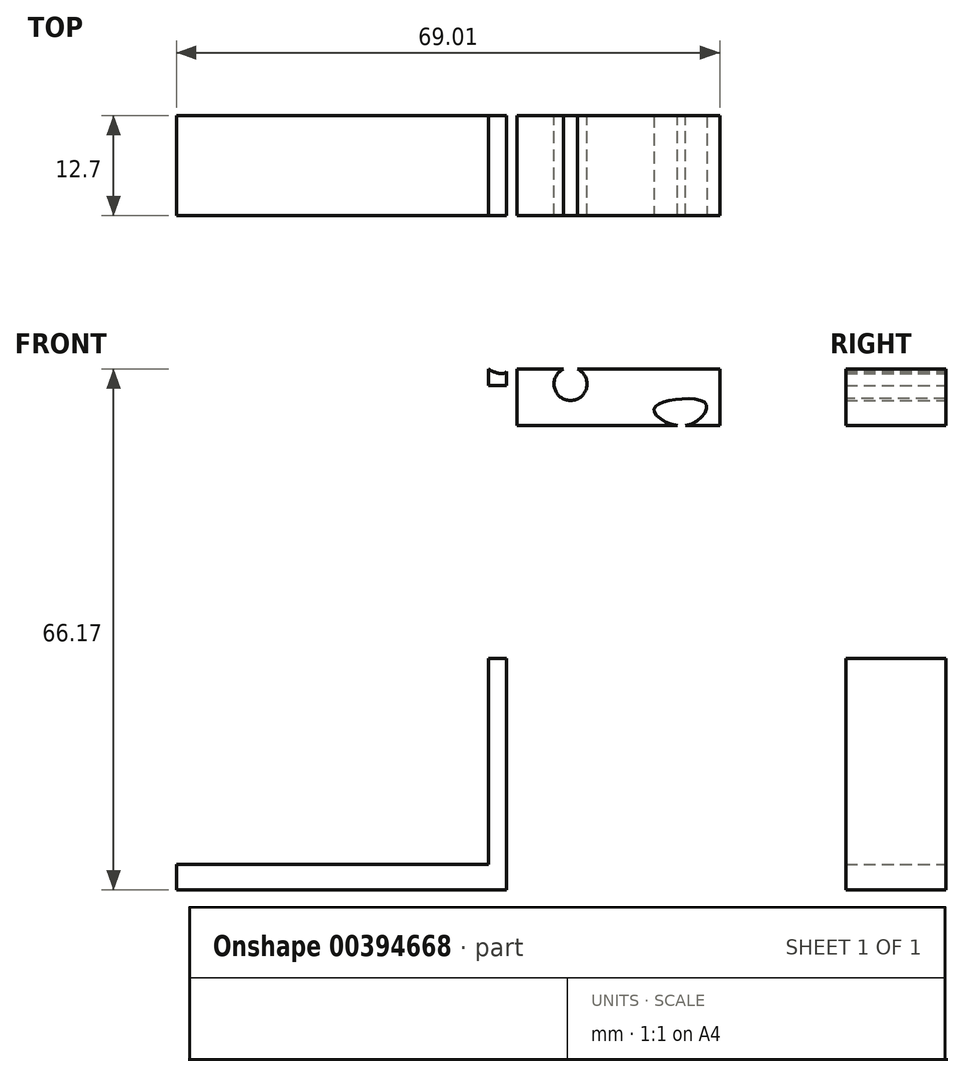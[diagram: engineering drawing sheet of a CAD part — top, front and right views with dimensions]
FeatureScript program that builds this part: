
annotation { "Feature Type Name" : "Feature", "Feature Type Description" : "" }
export const myFeature = defineFeature(function(context is Context, id is Id, definition is map)
    precondition{}
    {
        {
            var Q0;
            Q0=qCreatedBy(makeId("Front.planeOp"),FACE);
            var sketch = newSketch(context, id + "F0", { "sketchPlane" : qUnion([Q0])});
            skLineSegment(sketch, "E0.bottom", {"start": v(9.3, -1.7) * mm, "end": v(-32.61, -1.7) * mm});
            skLineSegment(sketch, "E0.top", {"start": v(9.3, 1.52) * mm, "end": v(-32.61, 1.52) * mm});
            skLineSegment(sketch, "E0.left", {"start": v(9.3, -1.7) * mm, "end": v(9.3, 1.52) * mm});
            skLineSegment(sketch, "E0.right", {"start": v(-32.61, -1.7) * mm, "end": v(-32.61, 1.52) * mm});
            skLineSegment(sketch, "E1.bottom", {"start": v(7.02, 3.98) * mm, "end": v(9.3, 3.98) * mm});
            skLineSegment(sketch, "E1.top", {"start": v(7.02, 27.68) * mm, "end": v(9.3, 27.68) * mm});
            skLineSegment(sketch, "E1.left", {"start": v(7.02, 3.98) * mm, "end": v(7.02, 27.68) * mm});
            skLineSegment(sketch, "E1.right", {"start": v(9.3, 3.98) * mm, "end": v(9.3, 27.68) * mm});
            skLineSegment(sketch, "E2.top", {"start": v(7.02, 1.52) * mm, "end": v(9.3, 1.52) * mm});
            skLineSegment(sketch, "E2.left", {"start": v(7.02, 3.98) * mm, "end": v(7.02, 1.52) * mm});
            skLineSegment(sketch, "E2.right", {"start": v(9.3, 3.98) * mm, "end": v(9.3, 1.52) * mm});
            skLineSegment(sketch, "E3.bottom", {"start": v(7.02, -1.7) * mm, "end": v(9.3, -1.7) * mm});
            skLineSegment(sketch, "E3.top", {"start": v(7.02, -1.7) * mm, "end": v(9.3, -1.7) * mm});
            skLineSegment(sketch, "E3.left", {"start": v(7.02, -1.7) * mm, "end": v(7.02, -1.7) * mm});
            skLineSegment(sketch, "E3.right", {"start": v(9.3, -1.7) * mm, "end": v(9.3, -1.7) * mm});
            skLineSegment(sketch, "E4.bottom", {"start": v(9.3, -1.7) * mm, "end": v(7.02, -1.7) * mm});
            skLineSegment(sketch, "E4.top", {"start": v(9.3, -24.65) * mm, "end": v(7.02, -24.65) * mm});
            skLineSegment(sketch, "E4.left", {"start": v(9.3, -1.7) * mm, "end": v(9.3, -24.65) * mm});
            skLineSegment(sketch, "E4.right", {"start": v(7.02, -1.7) * mm, "end": v(7.02, -24.65) * mm});
            skLineSegment(sketch, "E5.bottom", {"start": v(-32.61, -1.7) * mm, "end": v(-29.2, -1.7) * mm});
            skLineSegment(sketch, "E5.top", {"start": v(-32.61, -28.06) * mm, "end": v(-29.2, -28.06) * mm});
            skLineSegment(sketch, "E5.left", {"start": v(-32.61, -1.7) * mm, "end": v(-32.61, -28.06) * mm});
            skLineSegment(sketch, "E5.right", {"start": v(-29.2, -1.7) * mm, "end": v(-29.2, -28.06) * mm});
            skPoint(sketch, "E6.oppositeSnap0", {"position": v(7.02, 15.83) * mm});
            skLineSegment(sketch, "E6.bottom", {"start": v(9.3, 27.68) * mm, "end": v(7.02, 27.68) * mm});
            skLineSegment(sketch, "E6.top", {"start": v(9.3, 64.46) * mm, "end": v(7.02, 64.46) * mm});
            skLineSegment(sketch, "E6.left", {"start": v(9.3, 27.68) * mm, "end": v(9.3, 64.46) * mm});
            skLineSegment(sketch, "E6.right", {"start": v(7.02, 27.68) * mm, "end": v(7.02, 64.46) * mm});
            skLineSegment(sketch, "E7.bottom", {"start": v(12.51, 64.46) * mm, "end": v(36.4, 64.46) * mm});
            skLineSegment(sketch, "E7.top", {"start": v(12.51, 57.26) * mm, "end": v(36.4, 57.26) * mm});
            skLineSegment(sketch, "E7.left", {"start": v(12.51, 64.46) * mm, "end": v(12.51, 57.26) * mm});
            skLineSegment(sketch, "E7.right", {"start": v(36.4, 64.46) * mm, "end": v(36.4, 57.26) * mm});
            skLineSegment(sketch, "E8.bottom", {"start": v(12.51, 57.26) * mm, "end": v(10.62, 57.26) * mm});
            skLineSegment(sketch, "E8.top", {"start": v(12.51, 64.46) * mm, "end": v(10.62, 64.46) * mm});
            skLineSegment(sketch, "E8.left", {"start": v(12.51, 57.26) * mm, "end": v(12.51, 64.46) * mm});
            skLineSegment(sketch, "E8.right", {"start": v(10.62, 57.26) * mm, "end": v(10.62, 64.46) * mm});
            skLineSegment(sketch, "E9.bottom", {"start": v(7.02, 64.46) * mm, "end": v(9.3, 64.46) * mm});
            skLineSegment(sketch, "E9.top", {"start": v(7.02, 62.38) * mm, "end": v(9.3, 62.38) * mm});
            skLineSegment(sketch, "E9.left", {"start": v(7.02, 64.46) * mm, "end": v(7.02, 62.38) * mm});
            skLineSegment(sketch, "E9.right", {"start": v(9.3, 64.46) * mm, "end": v(9.3, 62.38) * mm});
            skFitSpline(sketch, "E10", {"points": [v(7.02, 64.46) * mm, v(2.28, 70.34) * mm, v(9.3, 64.46) * mm, v(7.02, 64.46) * mm]});
            skCircle(sketch, "E11", {"center": v(17.44, 62.57) * mm, "radius": 2.1 * mm});
            skFitSpline(sketch, "E12", {"points": [v(28.06, 59.15) * mm, v(32.04, 57.26) * mm, v(34.7, 59.91) * mm, v(30.15, 60.48) * mm, v(28.06, 59.15) * mm]});
            skSolve(sketch);
        }
        {
            var Q0;
            Q0=makeQuery(id+"F0.imprint","IMPRINT",FACE,{"disambiguationData":[TD([[makeQuery(id+"F0.imprint","IMPRINT",EDGE,{"derivedFrom":sQuery(id+"F0.wireOp",EDGE,"E6.bottom")}),-1.0]])]});
            var Q1;
            Q1=makeQuery(id+"F0.imprint","IMPRINT",FACE,{"disambiguationData":[TD([[makeQuery(id+"F0.imprint","IMPRINT",EDGE,{"derivedFrom":sQuery(id+"F0.wireOp",EDGE,"E1.left")}),-1.0]])]});
            var Q2;
            {var subQ0=sQuery(id+"F0.wireOp",EDGE,"E11");var subQ1=sQuery(id+"F0.wireOp",EDGE,"E7.bottom");var subQ2=makeQuery(id+"F0.imprint","INTERSECT",VERTEX,{"disambiguationData":[OD(0.0)],"derivedFrom":[subQ1,subQ0]});Q2=makeQuery(id+"F0.imprint","IMPRINT",FACE,{"disambiguationData":[TD([[makeQuery(id+"F0.imprint","IMPRINT",EDGE,{"disambiguationData":[TD([[subQ2,-1.0]])],"derivedFrom":subQ1}),-1.0]])]});}
            var Q3;
            {var subQ4=sQuery(id+"F0.wireOp",EDGE,"E7.right");Q3=makeQuery(id+"F0.imprint","IMPRINT",FACE,{"disambiguationData":[TD([[makeQuery(id+"F0.imprint","IMPRINT",EDGE,{"derivedFrom":subQ4}),-1.0]])]});}
            var Q4;
            {var subQ0=sQuery(id+"F0.wireOp",EDGE,"E9.bottom");Q4=makeQuery(id+"F0.imprint","IMPRINT",FACE,{"disambiguationData":[TD([[makeQuery(id+"F0.imprint","IMPRINT",EDGE,{"derivedFrom":subQ0}),1.0]])]});}
            var Q5;
            Q5=makeQuery(id+"F0.imprint","IMPRINT",FACE,{"disambiguationData":[TD([[makeQuery(id+"F0.imprint","IMPRINT",EDGE,{"derivedFrom":sQuery(id+"F0.wireOp",EDGE,"E8.bottom")}),-1.0]])]});
            var Q6;
            {var subQ0=sQuery(id+"F0.wireOp",EDGE,"E9.top");Q6=makeQuery(id+"F0.imprint","IMPRINT",FACE,{"disambiguationData":[TD([[makeQuery(id+"F0.imprint","IMPRINT",EDGE,{"derivedFrom":subQ0}),1.0]])]});}
            var Q7;
            Q7=makeQuery(id+"F0.imprint","IMPRINT",FACE,{"disambiguationData":[TD([[makeQuery(id+"F0.imprint","IMPRINT",EDGE,{"derivedFrom":sQuery(id+"F0.wireOp",EDGE,"E1.bottom")}),-1.0]])]});
            var Q8;
            Q8=makeQuery(id+"F0.imprint","IMPRINT",FACE,{"disambiguationData":[TD([[makeQuery(id+"F0.imprint","IMPRINT",EDGE,{"derivedFrom":sQuery(id+"F0.wireOp",EDGE,"E0.bottom")}),-1.0]])]});
            var Q9;
            {var subQ0=sQuery(id+"F0.wireOp",EDGE,"E12");var subQ1=sQuery(id+"F0.wireOp",EDGE,"E7.top");var subQ2=makeQuery(id+"F0.imprint","INTERSECT",VERTEX,{"disambiguationData":[OD(0.0)],"derivedFrom":[subQ1,subQ0]});Q9=makeQuery(id+"F0.imprint","IMPRINT",FACE,{"disambiguationData":[TD([[makeQuery(id+"F0.imprint","IMPRINT",EDGE,{"disambiguationData":[TD([[subQ2,-1.0]])],"derivedFrom":subQ1}),1.0]])]});}
            var Q10;
            Q10=makeQuery(id+"F0.imprint","IMPRINT",FACE,{"disambiguationData":[TD([[makeQuery(id+"F0.imprint","IMPRINT",EDGE,{"derivedFrom":sQuery(id+"F0.wireOp",EDGE,"E4.bottom")}),1.0]])]});
            var Q11;
            Q11=makeQuery(id+"F0.imprint","IMPRINT",FACE,{"disambiguationData":[TD([[makeQuery(id+"F0.imprint","IMPRINT",EDGE,{"derivedFrom":sQuery(id+"F0.wireOp",EDGE,"E5.bottom")}),-1.0]])]});
            extrude(context, id + "F1", {"entities" : qUnion([Q0, Q1, Q2, Q3, Q4, Q5, Q6, Q7, Q8, Q9, Q10, Q11]), "depth" : 12.7 * mm});
        }
    });
